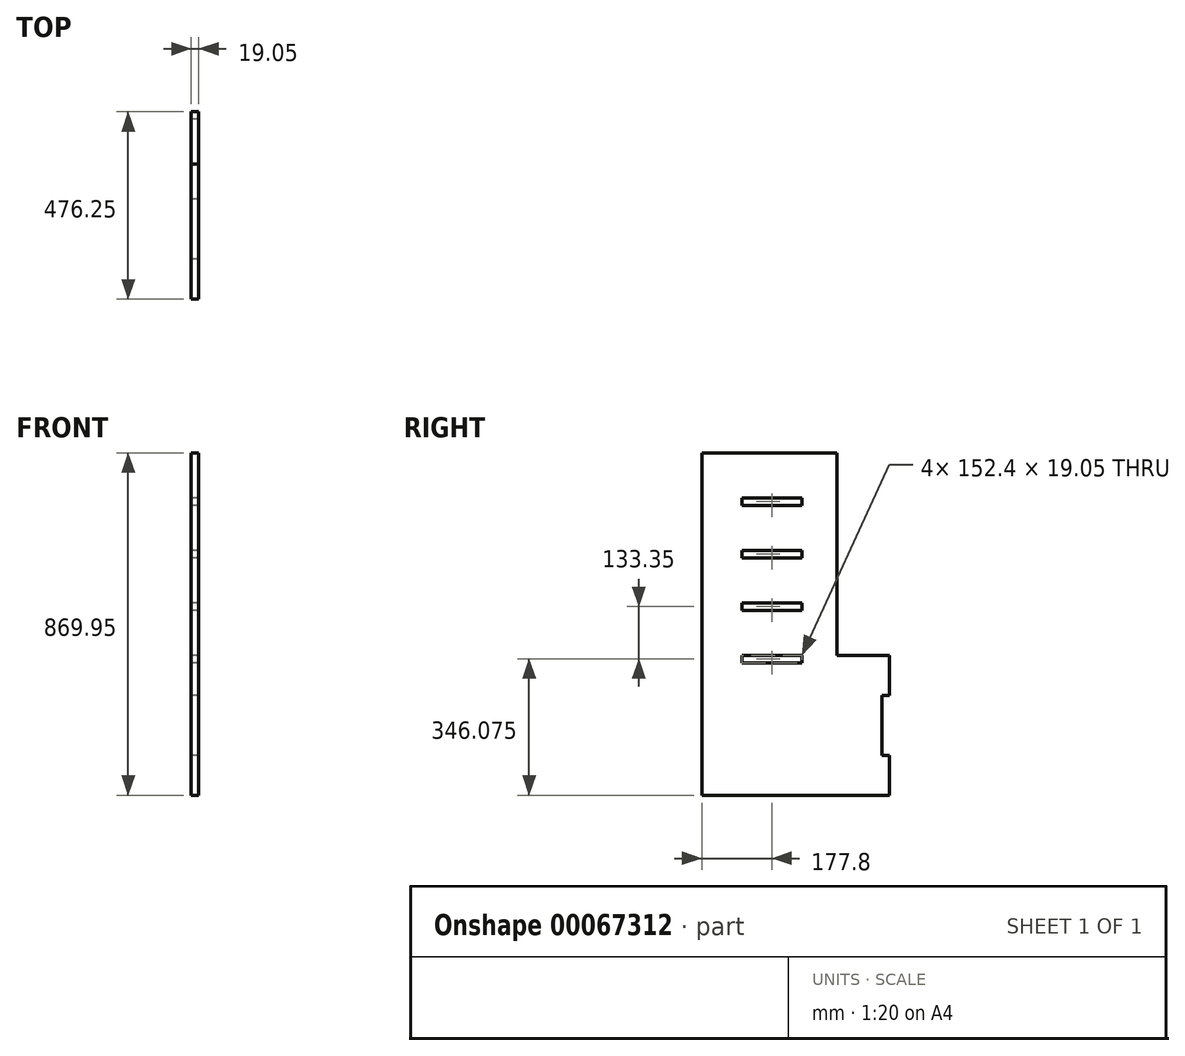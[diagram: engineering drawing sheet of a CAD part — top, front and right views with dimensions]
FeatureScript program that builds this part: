
annotation { "Feature Type Name" : "Feature", "Feature Type Description" : "" }
export const myFeature = defineFeature(function(context is Context, id is Id, definition is map)
    precondition{}
    {
        {
            var Q0;
            Q0=qCreatedBy(makeId("Right.planeOp"),FACE);
            var sketch = newSketch(context, id + "F0", { "sketchPlane" : qUnion([Q0])});
            skLineSegment(sketch, "E0.bottom", {"start": v(-171.45, 0) * mm, "end": v(171.45, 0) * mm});
            skLineSegment(sketch, "E0.top", {"start": v(-171.45, -869.95) * mm, "end": v(171.45, -869.95) * mm});
            skLineSegment(sketch, "E0.left", {"start": v(-171.45, 0) * mm, "end": v(-171.45, -869.95) * mm});
            skLineSegment(sketch, "E0.right", {"start": v(171.45, 0) * mm, "end": v(171.45, -869.95) * mm});
            skLineSegment(sketch, "E1.bottom", {"start": v(-69.85, -114.3) * mm, "end": v(82.55, -114.3) * mm});
            skLineSegment(sketch, "E1.top", {"start": v(-69.85, -133.35) * mm, "end": v(82.55, -133.35) * mm});
            skLineSegment(sketch, "E1.left", {"start": v(-69.85, -114.3) * mm, "end": v(-69.85, -133.35) * mm});
            skLineSegment(sketch, "E1.right", {"start": v(82.55, -114.3) * mm, "end": v(82.55, -133.35) * mm});
            skLineSegment(sketch, "E2.bottom", {"start": v(-69.85, -247.65) * mm, "end": v(82.55, -247.65) * mm});
            skLineSegment(sketch, "E2.top", {"start": v(-69.85, -266.7) * mm, "end": v(82.55, -266.7) * mm});
            skLineSegment(sketch, "E2.left", {"start": v(-69.85, -247.65) * mm, "end": v(-69.85, -266.7) * mm});
            skLineSegment(sketch, "E2.right", {"start": v(82.55, -247.65) * mm, "end": v(82.55, -266.7) * mm});
            skLineSegment(sketch, "E3.bottom", {"start": v(-69.85, -381) * mm, "end": v(82.55, -381) * mm});
            skLineSegment(sketch, "E4.bottom", {"start": v(-69.85, -514.35) * mm, "end": v(82.55, -514.35) * mm});
            skLineSegment(sketch, "E4.top", {"start": v(-69.85, -533.4) * mm, "end": v(82.55, -533.4) * mm});
            skLineSegment(sketch, "E4.left", {"start": v(-69.85, -514.35) * mm, "end": v(-69.85, -533.4) * mm});
            skLineSegment(sketch, "E4.right", {"start": v(82.55, -514.35) * mm, "end": v(82.55, -533.4) * mm});
            skLineSegment(sketch, "E5.bottom", {"start": v(-19.05, -869.95) * mm, "end": v(133.35, -869.95) * mm});
            skLineSegment(sketch, "E6.bottom", {"start": v(-19.05, -869.95) * mm, "end": v(40.36, -869.95) * mm});
            skLineSegment(sketch, "E7.top", {"start": v(-19.05, -889) * mm, "end": v(133.35, -889) * mm});
            skLineSegment(sketch, "E7.left", {"start": v(-19.05, -869.95) * mm, "end": v(-19.05, -889) * mm});
            skLineSegment(sketch, "E7.right", {"start": v(133.35, -869.95) * mm, "end": v(133.35, -889) * mm});
            skLineSegment(sketch, "E8", {"start": v(-69.85, -381) * mm, "end": v(-69.85, -400.05) * mm});
            skLineSegment(sketch, "E9", {"start": v(-69.85, -400.05) * mm, "end": v(82.55, -400.05) * mm});
            skLineSegment(sketch, "E10", {"start": v(82.55, -400.05) * mm, "end": v(82.55, -381) * mm});
            skLineSegment(sketch, "E11.bottom", {"start": v(171.45, -869.95) * mm, "end": v(304.8, -869.95) * mm});
            skLineSegment(sketch, "E11.top", {"start": v(171.45, -514.35) * mm, "end": v(304.8, -514.35) * mm});
            skLineSegment(sketch, "E11.left", {"start": v(171.45, -869.95) * mm, "end": v(171.45, -514.35) * mm});
            skLineSegment(sketch, "E11.right", {"start": v(304.8, -869.95) * mm, "end": v(304.8, -514.35) * mm});
            skLineSegment(sketch, "E12.bottom", {"start": v(304.8, -615.95) * mm, "end": v(285.75, -615.95) * mm});
            skLineSegment(sketch, "E12.top", {"start": v(304.8, -768.35) * mm, "end": v(285.75, -768.35) * mm});
            skLineSegment(sketch, "E12.left", {"start": v(304.8, -615.95) * mm, "end": v(304.8, -768.35) * mm});
            skLineSegment(sketch, "E12.right", {"start": v(285.75, -615.95) * mm, "end": v(285.75, -768.35) * mm});
            skLineSegment(sketch, "E13.bottom", {"start": v(-69.85, 0) * mm, "end": v(82.55, 0) * mm});
            skLineSegment(sketch, "E13.top", {"start": v(-69.85, 19.05) * mm, "end": v(82.55, 19.05) * mm});
            skLineSegment(sketch, "E13.left", {"start": v(-69.85, 0) * mm, "end": v(-69.85, 19.05) * mm});
            skLineSegment(sketch, "E13.right", {"start": v(82.55, 0) * mm, "end": v(82.55, 19.05) * mm});
            skSolve(sketch);
        }
        {
            var Q0;
            Q0=makeQuery(id+"F0.imprint","IMPRINT",FACE,{"disambiguationData":[TD([[makeQuery(id+"F0.imprint","IMPRINT",EDGE,{"derivedFrom":sQuery(id+"F0.wireOp",EDGE,"E0.bottom")}),-1.0]])]});
            var Q1;
            Q1=makeQuery(id+"F0.imprint","IMPRINT",FACE,{"disambiguationData":[TD([[makeQuery(id+"F0.imprint","IMPRINT",EDGE,{"derivedFrom":sQuery(id+"F0.wireOp",EDGE,"E5.bottom")}),-1.0]])]});
            var Q2;
            {var subQ3=sQuery(id+"F0.wireOp",EDGE,"a29a86c9-f4e7-4d65-be75-dea9e2e52950.bottom");Q2=makeQuery(id+"F0.imprint","IMPRINT",FACE,{"disambiguationData":[TD([[makeQuery(id+"F0.imprint","IMPRINT",EDGE,{"derivedFrom":subQ3}),-1.0]])]});}
            var Q3;
            {var subQ3=sQuery(id+"F0.wireOp",EDGE,"482b441b-516f-4dff-9e70-26fbe542cdff.bottom");Q3=makeQuery(id+"F0.imprint","IMPRINT",FACE,{"disambiguationData":[TD([[makeQuery(id+"F0.imprint","IMPRINT",EDGE,{"derivedFrom":subQ3}),-1.0]])]});}
            var Q4;
            Q4=makeQuery(id+"F0.imprint","IMPRINT",FACE,{"disambiguationData":[TD([[makeQuery(id+"F0.imprint","IMPRINT",EDGE,{"derivedFrom":sQuery(id+"F0.wireOp",EDGE,"a29a86c9-f4e7-4d65-be75-dea9e2e52950.top")}),1.0]])]});
            var Q5;
            Q5=makeQuery(id+"F0.imprint","IMPRINT",FACE,{"disambiguationData":[TD([[makeQuery(id+"F0.imprint","IMPRINT",EDGE,{"derivedFrom":sQuery(id+"F0.wireOp",EDGE,"2477f2b8-453e-48af-9c50-ee16ae39cff9.bottom")}),1.0]])]});
            var Q6;
            {var subQ0=sQuery(id+"F0.wireOp",EDGE,"482b441b-516f-4dff-9e70-26fbe542cdff.top");Q6=makeQuery(id+"F0.imprint","IMPRINT",FACE,{"disambiguationData":[TD([[makeQuery(id+"F0.imprint","IMPRINT",EDGE,{"derivedFrom":subQ0}),1.0]])]});}
            var Q7;
            Q7=makeQuery(id+"F0.imprint","IMPRINT",FACE,{"disambiguationData":[TD([[makeQuery(id+"F0.imprint","IMPRINT",EDGE,{"derivedFrom":sQuery(id+"F0.wireOp",EDGE,"962796bc-906d-4d0b-82fb-ca6226cb6b58.bottom")}),1.0]])]});
            var Q8;
            Q8=makeQuery(id+"F0.imprint","IMPRINT",FACE,{"disambiguationData":[TD([[makeQuery(id+"F0.imprint","IMPRINT",EDGE,{"derivedFrom":sQuery(id+"F0.wireOp",EDGE,"962796bc-906d-4d0b-82fb-ca6226cb6b58.top")}),-1.0]])]});
            var Q9;
            {var subQ3=sQuery(id+"F0.wireOp",EDGE,"9086a410-cb1b-4498-9778-83905ee574a5.bottom");Q9=makeQuery(id+"F0.imprint","IMPRINT",FACE,{"disambiguationData":[TD([[makeQuery(id+"F0.imprint","IMPRINT",EDGE,{"derivedFrom":subQ3}),1.0]])]});}
            var Q10;
            {var subQ1=sQuery(id+"F0.wireOp",EDGE,"E11.bottom");Q10=makeQuery(id+"F0.imprint","IMPRINT",FACE,{"disambiguationData":[TD([[makeQuery(id+"F0.imprint","IMPRINT",EDGE,{"derivedFrom":subQ1}),1.0]])]});}
            var Q11;
            Q11=makeQuery(id+"F0.imprint","IMPRINT",FACE,{"disambiguationData":[TD([[makeQuery(id+"F0.imprint","IMPRINT",EDGE,{"derivedFrom":sQuery(id+"F0.wireOp",EDGE,"E13.bottom")}),1.0]])]});
            extrude(context, id + "F1", {"entities" : qUnion([Q0, Q1, Q2, Q3, Q4, Q5, Q6, Q7, Q8, Q9, Q10, Q11]), "depth" : 19.05 * mm});
        }
    });
